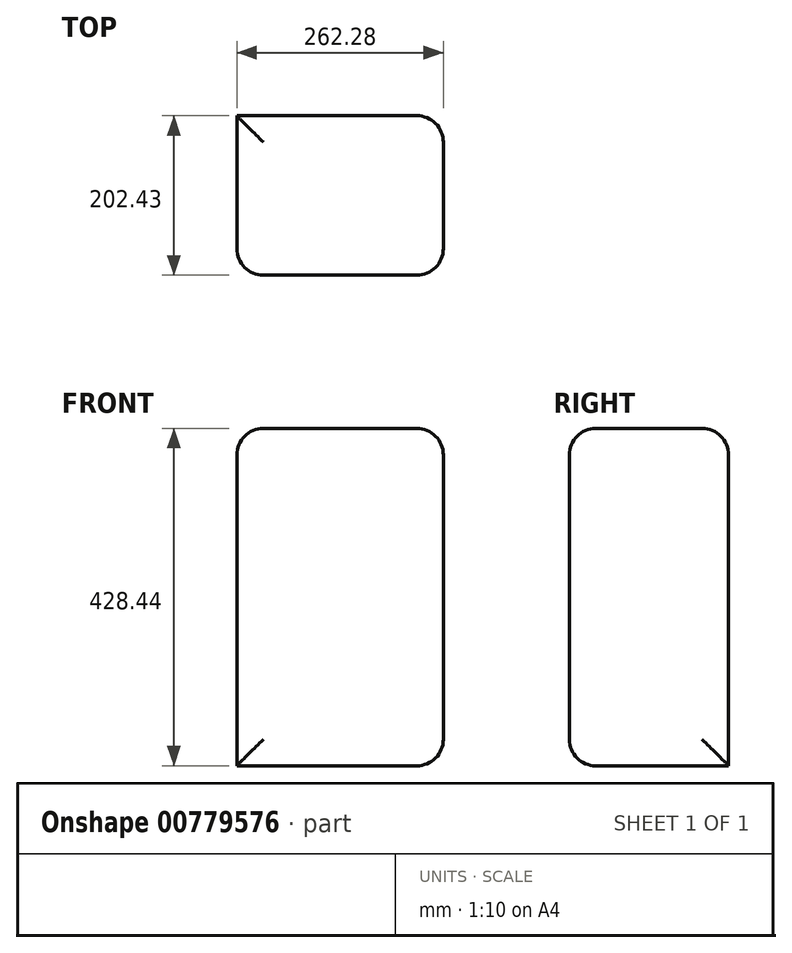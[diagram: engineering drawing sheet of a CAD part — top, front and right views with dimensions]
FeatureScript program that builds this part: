
annotation { "Feature Type Name" : "Feature", "Feature Type Description" : "" }
export const myFeature = defineFeature(function(context is Context, id is Id, definition is map)
    precondition{}
    {
        {
            var Q0;
            Q0=qCreatedBy(makeId("Right.planeOp"),FACE);
            var sketch = newSketch(context, id + "F0", { "sketchPlane" : qUnion([Q0])});
            skLineSegment(sketch, "E0.bottom", {"start": v(0, 0) * mm, "end": v(202.43, 0) * mm});
            skLineSegment(sketch, "E0.top", {"start": v(0, -428.44) * mm, "end": v(202.43, -428.44) * mm});
            skLineSegment(sketch, "E0.left", {"start": v(0, 0) * mm, "end": v(0, -428.44) * mm});
            skLineSegment(sketch, "E0.right", {"start": v(202.43, 0) * mm, "end": v(202.43, -428.44) * mm});
            skSolve(sketch);
        }
        {
            var Q0;
            Q0=makeQuery(id+"F0.imprint","IMPRINT",FACE,{"disambiguationData":[TD([[makeQuery(id+"F0.imprint","IMPRINT",EDGE,{"derivedFrom":sQuery(id+"F0.wireOp",EDGE,"E0.bottom")}),-1.0]])]});
            var Q1;
            Q1 = qSketchRegion(id + "F0", true);
            extrude(context, id + "F1", {"entities" : qUnion([Q0, Q1]), "depth" : 262.28 * mm, "offsetDistance" : 25 * mm});
        }
        {
            var Q0;
            Q0=makeQuery(id+"F1.opExtrude","SWEPT_FACE",FACE,{"disambiguationData":[OSD([sQuery(id+"F0.wireOp",EDGE,"E0.left")])]});
            var sketch = newSketch(context, id + "F2", { "sketchPlane" : qUnion([Q0])});
            skSolve(sketch);
        }
        {
            var Q0;
            Q0=makeQuery(id+"F1.opExtrude","CAP_FACE",FACE,{"disambiguationData":[OSD([sQuery(id+"F0.wireOp",EDGE,"E0.bottom"),sQuery(id+"F0.wireOp",EDGE,"E0.top"),sQuery(id+"F0.wireOp",EDGE,"E0.left"),sQuery(id+"F0.wireOp",EDGE,"E0.right")])],"isStart":false});
            var Q1;
            Q1=makeQuery(id+"F1.opExtrude","SWEPT_FACE",FACE,{"disambiguationData":[OSD([sQuery(id+"F0.wireOp",EDGE,"E0.left")])]});
            var Q2;
            Q2=makeQuery(id+"F1.opExtrude","SWEPT_FACE",FACE,{"disambiguationData":[OSD([sQuery(id+"F0.wireOp",EDGE,"E0.bottom")])]});
            fillet(context, id + "F3", {"entities" : qUnion([Q0, Q1, Q2]), "radius" : 33.6 * mm, "tangentPropagation" : true, "allowEdgeOverflow" : false});
        }
    });
